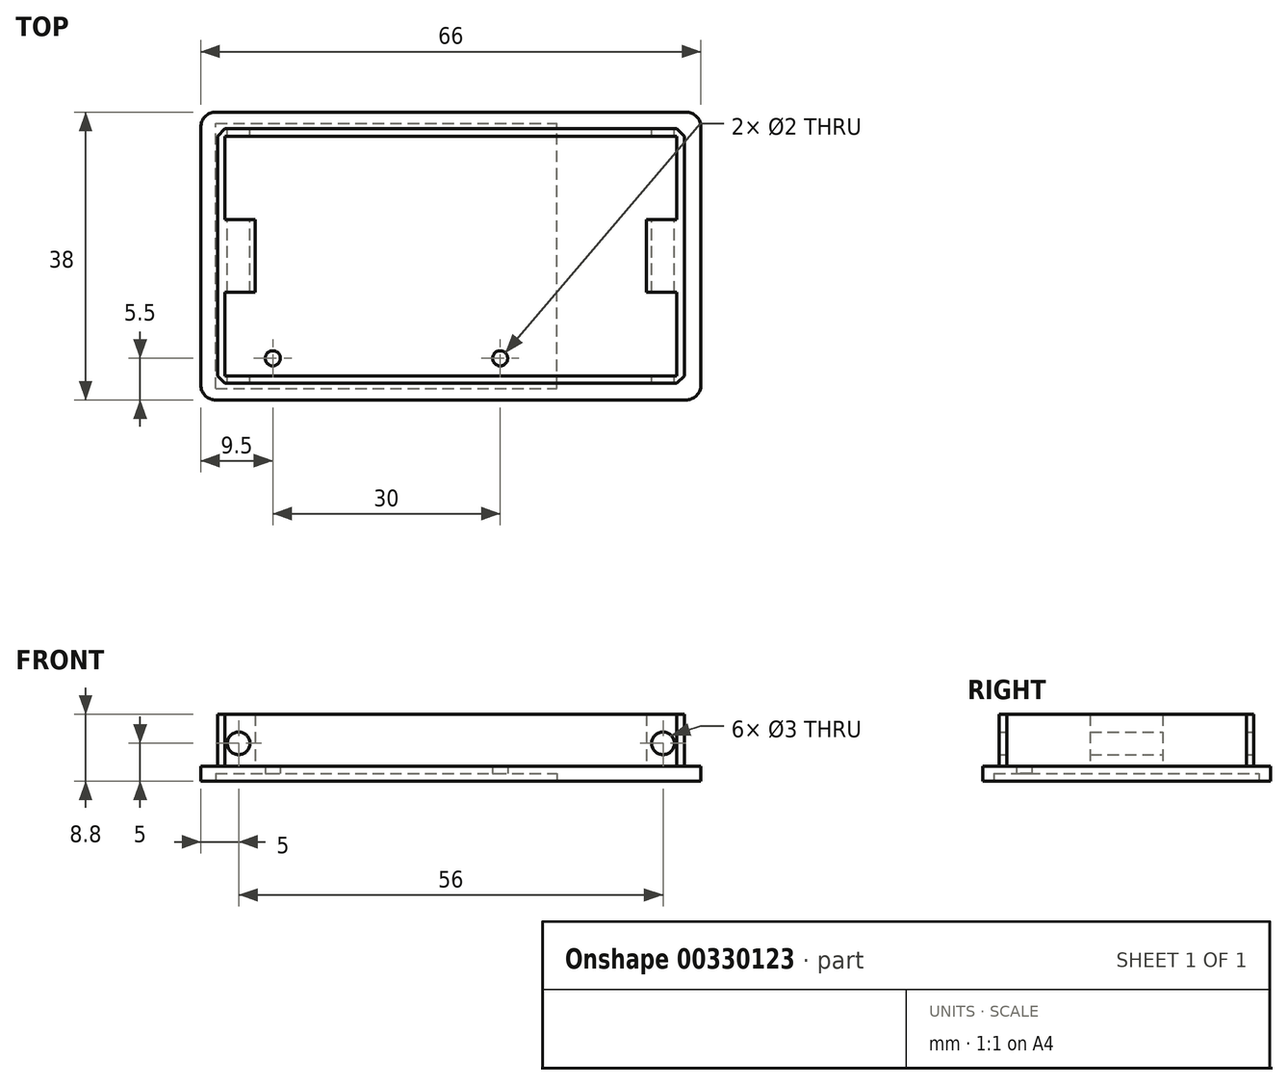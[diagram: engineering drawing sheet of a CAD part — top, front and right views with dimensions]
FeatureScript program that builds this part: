
annotation { "Feature Type Name" : "Feature", "Feature Type Description" : "" }
export const myFeature = defineFeature(function(context is Context, id is Id, definition is map)
    precondition{}
    {
        {
            var Q0;
            Q0=qCreatedBy(makeId("Top.planeOp"),FACE);
            var sketch = newSketch(context, id + "F0", { "sketchPlane" : qUnion([Q0])});
            skLineSegment(sketch, "E0.bottom", {"start": v(0, 0) * mm, "end": v(66, 0) * mm});
            skLineSegment(sketch, "E0.top", {"start": v(0, -38) * mm, "end": v(66, -38) * mm});
            skLineSegment(sketch, "E0.left", {"start": v(0, 0) * mm, "end": v(0, -38) * mm});
            skLineSegment(sketch, "E0.right", {"start": v(66, 0) * mm, "end": v(66, -38) * mm});
            skSolve(sketch);
        }
        {
            var Q0;
            Q0=qSketchRegion(id+"F0",true);
            extrude(context, id + "F1", {"entities" : qUnion([Q0]), "depth" : 2 * mm});
        }
        {
            var Q0;
            Q0=makeQuery(id+"F1.opExtrude","CAP_FACE",FACE,{"disambiguationData":[OSD([sQuery(id+"F0.wireOp",EDGE,"E0.bottom"),sQuery(id+"F0.wireOp",EDGE,"E0.top"),sQuery(id+"F0.wireOp",EDGE,"E0.left"),sQuery(id+"F0.wireOp",EDGE,"E0.right")])],"isStart":false});
            var sketch = newSketch(context, id + "F2", { "sketchPlane" : qUnion([Q0])});
            skLineSegment(sketch, "E1.bottom", {"start": v(2.2, -2.2) * mm, "end": v(63.8, -2.2) * mm});
            skLineSegment(sketch, "E1.top", {"start": v(2.2, -35.8) * mm, "end": v(63.8, -35.8) * mm});
            skLineSegment(sketch, "E1.left", {"start": v(2.2, -2.2) * mm, "end": v(2.2, -35.8) * mm});
            skLineSegment(sketch, "E1.right", {"start": v(63.8, -2.2) * mm, "end": v(63.8, -35.8) * mm});
            skLineSegment(sketch, "E2.bottom", {"start": v(3.2, -3.2) * mm, "end": v(62.8, -3.2) * mm});
            skLineSegment(sketch, "E2.top", {"start": v(3.2, -34.8) * mm, "end": v(62.8, -34.8) * mm});
            skLineSegment(sketch, "E2.left", {"start": v(3.2, -3.2) * mm, "end": v(3.2, -34.8) * mm});
            skLineSegment(sketch, "E2.right", {"start": v(62.8, -3.2) * mm, "end": v(62.8, -34.8) * mm});
            skSolve(sketch);
        }
        {
            var Q0;
            Q0=qSketchRegion(id+"F2",true);
            extrude(context, id + "F3", {"entities" : qUnion([Q0]), "operationType" : NewBodyOperationType.ADD, "depth" : 6.8 * mm});
        }
        {
            var Q0;
            Q0=makeQuery(id+"F1.opExtrude","SWEPT_EDGE",EDGE,{"disambiguationData":[OSD([sQuery(id+"F0.wireOp",EDGE,"E0.top"),sQuery(id+"F0.wireOp",EDGE,"E0.left")])]});
            var Q1;
            Q1=makeQuery(id+"F1.opExtrude","SWEPT_EDGE",EDGE,{"disambiguationData":[OSD([sQuery(id+"F0.wireOp",EDGE,"E0.bottom"),sQuery(id+"F0.wireOp",EDGE,"E0.left")])]});
            var Q2;
            Q2=makeQuery(id+"F1.opExtrude","SWEPT_EDGE",EDGE,{"disambiguationData":[OSD([sQuery(id+"F0.wireOp",EDGE,"E0.top"),sQuery(id+"F0.wireOp",EDGE,"E0.right")])]});
            var Q3;
            Q3=makeQuery(id+"F1.opExtrude","SWEPT_EDGE",EDGE,{"disambiguationData":[OSD([sQuery(id+"F0.wireOp",EDGE,"E0.bottom"),sQuery(id+"F0.wireOp",EDGE,"E0.right")])]});
            fillet(context, id + "F4", {"entities" : qUnion([Q0, Q1, Q2, Q3]), "radius" : 2 * mm, "tangentPropagation" : true, "allowEdgeOverflow" : false});
        }
        {
            var Q0;
            Q0=makeQuery(id+"F1.opExtrude","CAP_FACE",FACE,{"disambiguationData":[OSD([sQuery(id+"F0.wireOp",EDGE,"E0.bottom"),sQuery(id+"F0.wireOp",EDGE,"E0.top"),sQuery(id+"F0.wireOp",EDGE,"E0.left"),sQuery(id+"F0.wireOp",EDGE,"E0.right")])],"isStart":true});
            var sketch = newSketch(context, id + "F5", { "sketchPlane" : qUnion([Q0])});
            skLineSegment(sketch, "E3.bottom", {"start": v(2, 36.5) * mm, "end": v(47, 36.5) * mm});
            skLineSegment(sketch, "E3.top", {"start": v(2, 1.5) * mm, "end": v(47, 1.5) * mm});
            skLineSegment(sketch, "E3.left", {"start": v(2, 36.5) * mm, "end": v(2, 1.5) * mm});
            skLineSegment(sketch, "E3.right", {"start": v(47, 36.5) * mm, "end": v(47, 1.5) * mm});
            skSolve(sketch);
        }
        {
            var Q0;
            Q0=qSketchRegion(id+"F5",true);
            extrude(context, id + "F6", {"entities" : qUnion([Q0]), "operationType" : NewBodyOperationType.REMOVE, "oppositeDirection" : true, "depth" : 1 * mm});
        }
        {
            var Q0;
            Q0=makeQuery(id+"F1.opExtrude","CAP_FACE",FACE,{"disambiguationData":[OSD([sQuery(id+"F0.wireOp",EDGE,"E0.bottom"),sQuery(id+"F0.wireOp",EDGE,"E0.top"),sQuery(id+"F0.wireOp",EDGE,"E0.left"),sQuery(id+"F0.wireOp",EDGE,"E0.right")])],"isStart":true});
            var sketch = newSketch(context, id + "F7", { "sketchPlane" : qUnion([Q0])});
            skCircle(sketch, "E4", {"center": v(9.5, 32.5) * mm, "radius": 1 * mm});
            skCircle(sketch, "E5", {"center": v(39.5, 32.5) * mm, "radius": 1 * mm});
            skSolve(sketch);
        }
        {
            var Q0;
            Q0=qSketchRegion(id+"F7",true);
            extrude(context, id + "F8", {"entities" : qUnion([Q0]), "operationType" : NewBodyOperationType.REMOVE, "endBound" : BoundingType.THROUGH_ALL, "oppositeDirection" : true, "depth" : 25 * mm});
        }
        {
            var Q0;
            Q0=makeQuery(id+"F3.boolean.opBoolean","SPLIT",FACE,{"disambiguationData":[TD([makeQuery(id+"F3.opExtrude","SWEPT_FACE",FACE,{"disambiguationData":[OSD([sQuery(id+"F2.wireOp",EDGE,"E2.bottom")])]})])],"derivedFrom":makeQuery(id+"F1.opExtrude","CAP_FACE",FACE,{"disambiguationData":[OSD([sQuery(id+"F0.wireOp",EDGE,"E0.bottom"),sQuery(id+"F0.wireOp",EDGE,"E0.top"),sQuery(id+"F0.wireOp",EDGE,"E0.left"),sQuery(id+"F0.wireOp",EDGE,"E0.right")])],"isStart":false})});
            var sketch = newSketch(context, id + "F9", { "sketchPlane" : qUnion([Q0])});
            skLineSegment(sketch, "E6.bottom", {"start": v(3.2, -14.2) * mm, "end": v(7.2, -14.2) * mm});
            skLineSegment(sketch, "E6.top", {"start": v(3.2, -23.8) * mm, "end": v(7.2, -23.8) * mm});
            skLineSegment(sketch, "E6.left", {"start": v(3.2, -14.2) * mm, "end": v(3.2, -23.8) * mm});
            skLineSegment(sketch, "E6.right", {"start": v(7.2, -14.2) * mm, "end": v(7.2, -23.8) * mm});
            skLineSegment(sketch, "E7.bottom", {"start": v(58.8, -14.2) * mm, "end": v(62.8, -14.2) * mm});
            skLineSegment(sketch, "E7.top", {"start": v(58.8, -23.8) * mm, "end": v(62.8, -23.8) * mm});
            skLineSegment(sketch, "E7.left", {"start": v(58.8, -14.2) * mm, "end": v(58.8, -23.8) * mm});
            skLineSegment(sketch, "E7.right", {"start": v(62.8, -14.2) * mm, "end": v(62.8, -23.8) * mm});
            skSolve(sketch);
        }
        {
            var Q0;
            Q0 = qSketchRegion(id + "F9", true);
            extrude(context, id + "F10", {"entities" : qUnion([Q0]), "operationType" : NewBodyOperationType.ADD, "depth" : 6.8 * mm});
        }
        {
            var Q0;
            Q0=makeQuery(id+"F3.opExtrude","SWEPT_FACE",FACE,{"disambiguationData":[OSD([sQuery(id+"F2.wireOp",EDGE,"E1.bottom")])]});
            var sketch = newSketch(context, id + "F11", { "sketchPlane" : qUnion([Q0])});
            skCircle(sketch, "E8", {"center": v(-61, 5) * mm, "radius": 1.5 * mm});
            skCircle(sketch, "E9", {"center": v(-5, 5) * mm, "radius": 1.5 * mm});
            skSolve(sketch);
        }
        {
            var Q0;
            Q0=qSketchRegion(id+"F11",true);
            extrude(context, id + "F12", {"entities" : qUnion([Q0]), "operationType" : NewBodyOperationType.REMOVE, "endBound" : BoundingType.THROUGH_ALL, "oppositeDirection" : true, "depth" : 25 * mm});
        }
        {
            var Q0;
            Q0=makeQuery(id+"F3.opExtrude","SWEPT_EDGE",EDGE,{"disambiguationData":[OSD([sQuery(id+"F2.wireOp",EDGE,"E1.bottom"),sQuery(id+"F2.wireOp",EDGE,"E1.left")])]});
            var Q1;
            Q1=makeQuery(id+"F3.opExtrude","SWEPT_EDGE",EDGE,{"disambiguationData":[OSD([sQuery(id+"F2.wireOp",EDGE,"E1.top"),sQuery(id+"F2.wireOp",EDGE,"E1.left")])]});
            var Q2;
            Q2=makeQuery(id+"F3.opExtrude","SWEPT_EDGE",EDGE,{"disambiguationData":[OSD([sQuery(id+"F2.wireOp",EDGE,"E1.top"),sQuery(id+"F2.wireOp",EDGE,"E1.right")])]});
            var Q3;
            Q3=makeQuery(id+"F3.opExtrude","SWEPT_EDGE",EDGE,{"disambiguationData":[OSD([sQuery(id+"F2.wireOp",EDGE,"E1.bottom"),sQuery(id+"F2.wireOp",EDGE,"E1.right")])]});
            chamfer(context, id + "F13", {"entities" : qUnion([Q0, Q1, Q2, Q3]), "width" : 1 * mm, "tangentPropagation" : true});
        }
    });
